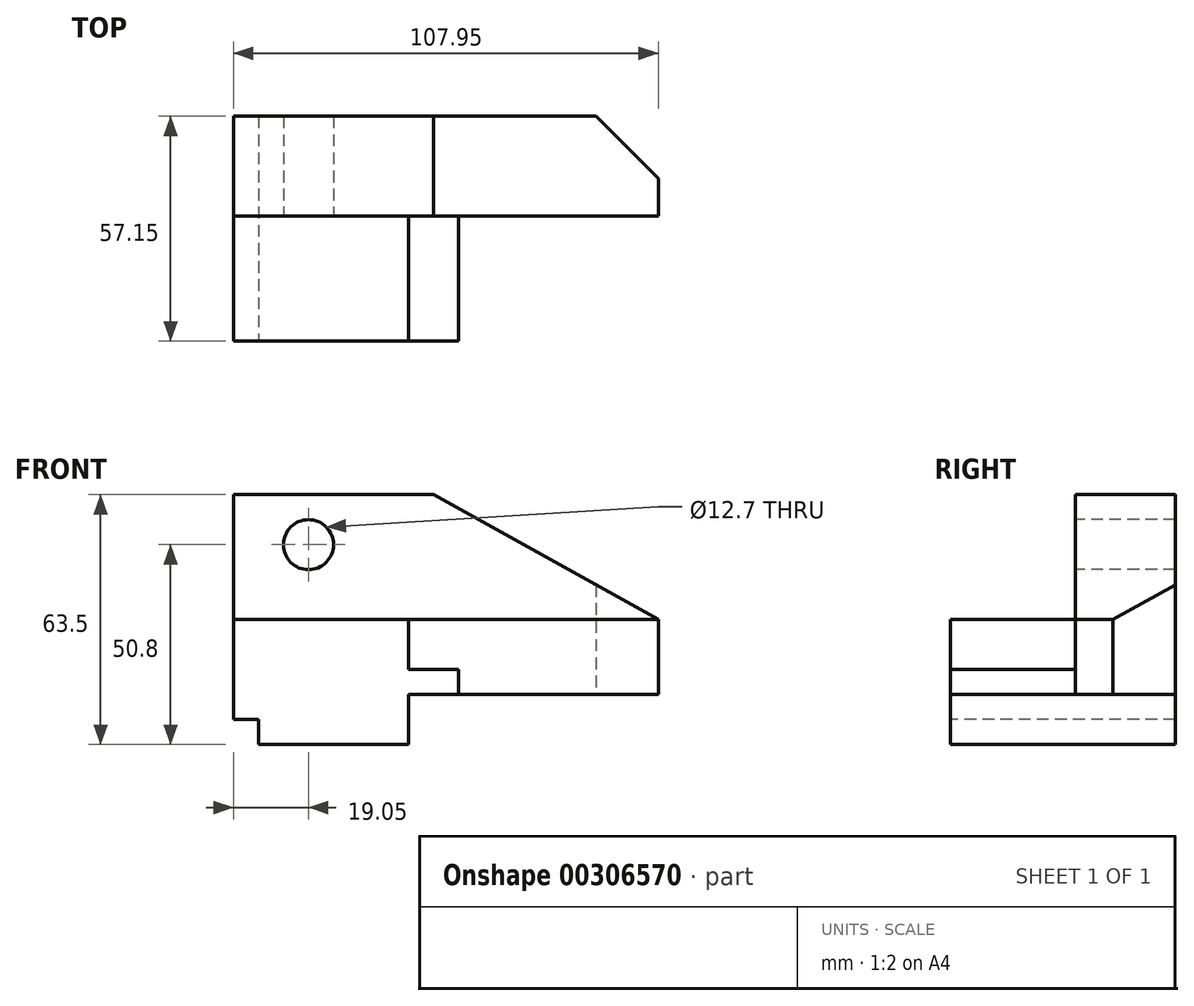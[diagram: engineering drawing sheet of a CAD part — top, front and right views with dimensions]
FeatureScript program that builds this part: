
annotation { "Feature Type Name" : "Feature", "Feature Type Description" : "" }
export const myFeature = defineFeature(function(context is Context, id is Id, definition is map)
    precondition{}
    {
        {
            var Q0;
            Q0=qCreatedBy(makeId("Front.planeOp"),FACE);
            var sketch = newSketch(context, id + "F0", { "sketchPlane" : qUnion([Q0])});
            skLineSegment(sketch, "E0.bottom", {"start": v(0, 0) * mm, "end": v(107.95, 0) * mm});
            skLineSegment(sketch, "E0.top", {"start": v(0, 63.5) * mm, "end": v(107.95, 63.5) * mm});
            skLineSegment(sketch, "E0.left", {"start": v(0, 0) * mm, "end": v(0, 63.5) * mm});
            skLineSegment(sketch, "E0.right", {"start": v(107.95, 0) * mm, "end": v(107.95, 63.5) * mm});
            skSolve(sketch);
        }
        {
            var Q0;
            Q0=makeQuery(id+"F0.imprint","IMPRINT",FACE,{"disambiguationData":[TD([[makeQuery(id+"F0.imprint","IMPRINT",EDGE,{"derivedFrom":sQuery(id+"F0.wireOp",EDGE,"E0.bottom")}),1.0]])]});
            extrude(context, id + "F1", {"entities" : qUnion([Q0]), "depth" : 57.15 * mm});
        }
        {
            var Q0;
            Q0=makeQuery(id+"F1.opExtrude","CAP_FACE",FACE,{"disambiguationData":[OSD([sQuery(id+"F0.wireOp",EDGE,"E0.bottom"),sQuery(id+"F0.wireOp",EDGE,"E0.top"),sQuery(id+"F0.wireOp",EDGE,"E0.left"),sQuery(id+"F0.wireOp",EDGE,"E0.right")])],"isStart":false});
            var sketch = newSketch(context, id + "F2", { "sketchPlane" : qUnion([Q0])});
            skLineSegment(sketch, "E1.bottom", {"start": v(0, 0) * mm, "end": v(6.35, 0) * mm});
            skLineSegment(sketch, "E1.top", {"start": v(0, 6.35) * mm, "end": v(6.35, 6.35) * mm});
            skLineSegment(sketch, "E1.left", {"start": v(0, 0) * mm, "end": v(0, 6.35) * mm});
            skLineSegment(sketch, "E1.right", {"start": v(6.35, 0) * mm, "end": v(6.35, 6.35) * mm});
            skSolve(sketch);
        }
        {
            var Q0;
            Q0 = qSketchRegion(id + "F2", true);
            extrude(context, id + "F3", {"entities" : qUnion([Q0]), "operationType" : NewBodyOperationType.REMOVE, "endBound" : BoundingType.THROUGH_ALL, "oppositeDirection" : true, "depth" : 25.4 * mm});
        }
        {
            var Q0;
            Q0=makeQuery(id+"F1.opExtrude","CAP_FACE",FACE,{"disambiguationData":[OSD([sQuery(id+"F0.wireOp",EDGE,"E0.bottom"),sQuery(id+"F0.wireOp",EDGE,"E0.top"),sQuery(id+"F0.wireOp",EDGE,"E0.left"),sQuery(id+"F0.wireOp",EDGE,"E0.right")])],"isStart":false});
            var sketch = newSketch(context, id + "F4", { "sketchPlane" : qUnion([Q0])});
            skLineSegment(sketch, "E2.bottom", {"start": v(107.95, 0) * mm, "end": v(44.45, 0) * mm});
            skLineSegment(sketch, "E2.top", {"start": v(107.95, 12.7) * mm, "end": v(44.45, 12.7) * mm});
            skLineSegment(sketch, "E2.left", {"start": v(107.95, 0) * mm, "end": v(107.95, 12.7) * mm});
            skLineSegment(sketch, "E2.right", {"start": v(44.45, 0) * mm, "end": v(44.45, 12.7) * mm});
            skSolve(sketch);
        }
        {
            var Q0;
            Q0 = qSketchRegion(id + "F4", true);
            extrude(context, id + "F5", {"entities" : qUnion([Q0]), "operationType" : NewBodyOperationType.REMOVE, "endBound" : BoundingType.THROUGH_ALL, "oppositeDirection" : true, "depth" : 25.4 * mm});
        }
        {
            var Q0;
            Q0=makeQuery(id+"F1.opExtrude","SWEPT_FACE",FACE,{"disambiguationData":[OSD([sQuery(id+"F0.wireOp",EDGE,"E0.right")])]});
            var sketch = newSketch(context, id + "F6", { "sketchPlane" : qUnion([Q0])});
            skLineSegment(sketch, "E3.bottom", {"start": v(-57.15, 63.5) * mm, "end": v(-25.39, 63.5) * mm});
            skLineSegment(sketch, "E3.top", {"start": v(-57.15, 31.75) * mm, "end": v(-25.39, 31.75) * mm});
            skLineSegment(sketch, "E3.left", {"start": v(-57.15, 63.5) * mm, "end": v(-57.15, 31.75) * mm});
            skLineSegment(sketch, "E3.right", {"start": v(-25.39, 63.5) * mm, "end": v(-25.39, 31.75) * mm});
            skSolve(sketch);
        }
        {
            var Q0;
            Q0 = qSketchRegion(id + "F6", true);
            extrude(context, id + "F7", {"entities" : qUnion([Q0]), "operationType" : NewBodyOperationType.REMOVE, "endBound" : BoundingType.THROUGH_ALL, "oppositeDirection" : true, "depth" : 25.4 * mm});
        }
        {
            var Q0;
            Q0=makeQuery(id+"F1.opExtrude","CAP_FACE",FACE,{"disambiguationData":[OSD([sQuery(id+"F0.wireOp",EDGE,"E0.bottom"),sQuery(id+"F0.wireOp",EDGE,"E0.top"),sQuery(id+"F0.wireOp",EDGE,"E0.left"),sQuery(id+"F0.wireOp",EDGE,"E0.right")])],"isStart":false});
            var sketch = newSketch(context, id + "F8", { "sketchPlane" : qUnion([Q0])});
            skLineSegment(sketch, "E4.bottom", {"start": v(44.45, 19.05) * mm, "end": v(57.15, 19.05) * mm});
            skLineSegment(sketch, "E4.top", {"start": v(44.45, 31.75) * mm, "end": v(57.15, 31.75) * mm});
            skLineSegment(sketch, "E4.left", {"start": v(44.45, 19.05) * mm, "end": v(44.45, 31.75) * mm});
            skLineSegment(sketch, "E4.right", {"start": v(57.15, 19.05) * mm, "end": v(57.15, 31.75) * mm});
            skSolve(sketch);
        }
        {
            var Q0;
            Q0 = qSketchRegion(id + "F8", true);
            extrude(context, id + "F9", {"entities" : qUnion([Q0]), "operationType" : NewBodyOperationType.REMOVE, "oppositeDirection" : true, "depth" : 31.75 * mm});
        }
        {
            var Q0;
            Q0=makeQuery(id+"F1.opExtrude","CAP_FACE",FACE,{"disambiguationData":[OSD([sQuery(id+"F0.wireOp",EDGE,"E0.bottom"),sQuery(id+"F0.wireOp",EDGE,"E0.top"),sQuery(id+"F0.wireOp",EDGE,"E0.left"),sQuery(id+"F0.wireOp",EDGE,"E0.right")])],"isStart":false});
            var sketch = newSketch(context, id + "F10", { "sketchPlane" : qUnion([Q0])});
            skLineSegment(sketch, "E5.bottom", {"start": v(57.15, 19.05) * mm, "end": v(107.95, 19.05) * mm});
            skLineSegment(sketch, "E5.top", {"start": v(57.15, 31.75) * mm, "end": v(107.95, 31.75) * mm});
            skLineSegment(sketch, "E5.left", {"start": v(57.15, 19.05) * mm, "end": v(57.15, 31.75) * mm});
            skLineSegment(sketch, "E5.right", {"start": v(107.95, 19.05) * mm, "end": v(107.95, 31.75) * mm});
            skSolve(sketch);
        }
        {
            var Q0;
            Q0 = qSketchRegion(id + "F10", true);
            extrude(context, id + "F11", {"entities" : qUnion([Q0]), "operationType" : NewBodyOperationType.REMOVE, "oppositeDirection" : true, "depth" : 31.75 * mm});
        }
        {
            var Q0;
            Q0=makeQuery(id+"F1.opExtrude","CAP_FACE",FACE,{"disambiguationData":[OSD([sQuery(id+"F0.wireOp",EDGE,"E0.bottom"),sQuery(id+"F0.wireOp",EDGE,"E0.top"),sQuery(id+"F0.wireOp",EDGE,"E0.left"),sQuery(id+"F0.wireOp",EDGE,"E0.right")])],"isStart":true});
            var sketch = newSketch(context, id + "F12", { "sketchPlane" : qUnion([Q0])});
            skLineSegment(sketch, "E6", {"start": v(-107.95, 12.7) * mm, "end": v(-107.95, 31.75) * mm});
            skLineSegment(sketch, "E7", {"start": v(-107.95, 31.75) * mm, "end": v(-50.8, 63.5) * mm});
            skLineSegment(sketch, "E8", {"start": v(-50.8, 63.5) * mm, "end": v(0, 63.5) * mm});
            skLineSegment(sketch, "E9", {"start": v(-107.95, 31.75) * mm, "end": v(-107.95, 63.5) * mm});
            skLineSegment(sketch, "E10", {"start": v(-107.95, 63.5) * mm, "end": v(-50.8, 63.5) * mm});
            skSolve(sketch);
        }
        {
            var Q0;
            Q0 = qSketchRegion(id + "F12", true);
            extrude(context, id + "F13", {"entities" : qUnion([Q0]), "operationType" : NewBodyOperationType.REMOVE, "endBound" : BoundingType.THROUGH_ALL, "oppositeDirection" : true, "depth" : 25.4 * mm});
        }
        {
            var Q0;
            Q0=makeQuery(id+"F5.boolean.opBoolean","COPY",FACE,{"derivedFrom":makeQuery(id+"F5.opExtrude","SWEPT_FACE",FACE,{"disambiguationData":[OSD([sQuery(id+"F4.wireOp",EDGE,"E2.top")])]})});
            var sketch = newSketch(context, id + "F14", { "sketchPlane" : qUnion([Q0])});
            skLineSegment(sketch, "E11", {"start": v(107.95, 0) * mm, "end": v(92.08, 0) * mm});
            skLineSegment(sketch, "E12", {"start": v(92.08, 0) * mm, "end": v(107.95, 15.87) * mm});
            skLineSegment(sketch, "E13", {"start": v(107.95, 15.88) * mm, "end": v(107.95, 0) * mm});
            skSolve(sketch);
        }
        {
            var Q0;
            Q0 = qSketchRegion(id + "F14", true);
            var Q1;
            Q1 = qConstructionFilter(qBodyType(qCreatedBy(id + "F14" ,EDGE), BodyType.WIRE), ConstructionObject.NO);
            extrude(context, id + "F15", {"entities" : qUnion([Q0]), "operationType" : NewBodyOperationType.REMOVE, "surfaceEntities" : qUnion([Q1]), "endBound" : BoundingType.THROUGH_ALL, "oppositeDirection" : true, "depth" : 25.4 * mm});
        }
        {
            var Q0;
            Q0=makeQuery(id+"F7.boolean.opBoolean","COPY",FACE,{"derivedFrom":makeQuery(id+"F7.opExtrude","SWEPT_FACE",FACE,{"disambiguationData":[OSD([sQuery(id+"F6.wireOp",EDGE,"E3.right")])]})});
            var sketch = newSketch(context, id + "F16", { "sketchPlane" : qUnion([Q0])});
            skCircle(sketch, "E14", {"center": v(19.05, 50.8) * mm, "radius": 6.35 * mm});
            skSolve(sketch);
        }
        {
            var Q0;
            Q0 = qSketchRegion(id + "F16", true);
            extrude(context, id + "F17", {"entities" : qUnion([Q0]), "operationType" : NewBodyOperationType.REMOVE, "endBound" : BoundingType.THROUGH_ALL, "oppositeDirection" : true, "depth" : 25.4 * mm});
        }
        {
            var Q0;
            Q0=makeQuery(id+"F11.boolean.opBoolean","MERGE",FACE,{"derivedFrom":[makeQuery(id+"F9.boolean.opBoolean","COPY",FACE,{"derivedFrom":makeQuery(id+"F9.opExtrude","SWEPT_FACE",FACE,{"disambiguationData":[OSD([sQuery(id+"F8.wireOp",EDGE,"E4.bottom")])]})}),makeQuery(id+"F11.opExtrude","SWEPT_FACE",FACE,{"disambiguationData":[OSD([sQuery(id+"F10.wireOp",EDGE,"E5.bottom")])]})]});
            var sketch = newSketch(context, id + "F18", { "sketchPlane" : qUnion([Q0])});
            skLineSegment(sketch, "E15.bottom", {"start": v(44.45, -57.15) * mm, "end": v(57.15, -57.15) * mm});
            skLineSegment(sketch, "E15.top", {"start": v(44.45, -25.4) * mm, "end": v(57.15, -25.4) * mm});
            skLineSegment(sketch, "E15.left", {"start": v(44.45, -57.15) * mm, "end": v(44.45, -25.4) * mm});
            skLineSegment(sketch, "E15.right", {"start": v(57.15, -57.15) * mm, "end": v(57.15, -25.4) * mm});
            skLineSegment(sketch, "E16.bottom", {"start": v(57.15, -25.4) * mm, "end": v(107.95, -25.4) * mm});
            skLineSegment(sketch, "E16.top", {"start": v(57.15, -57.15) * mm, "end": v(107.95, -57.15) * mm});
            skLineSegment(sketch, "E16.left", {"start": v(57.15, -25.4) * mm, "end": v(57.15, -57.15) * mm});
            skLineSegment(sketch, "E16.right", {"start": v(107.95, -25.4) * mm, "end": v(107.95, -57.15) * mm});
            skSolve(sketch);
        }
        {
            var Q0;
            Q0=makeQuery(id+"F18.imprint","IMPRINT",FACE,{"disambiguationData":[TD([[makeQuery(id+"F18.imprint","IMPRINT",EDGE,{"derivedFrom":sQuery(id+"F18.wireOp",EDGE,"E16.bottom")}),-1.0]])]});
            extrude(context, id + "F19", {"entities" : qUnion([Q0]), "operationType" : NewBodyOperationType.REMOVE, "endBound" : BoundingType.THROUGH_ALL, "oppositeDirection" : true, "depth" : 25.4 * mm});
        }
    });
